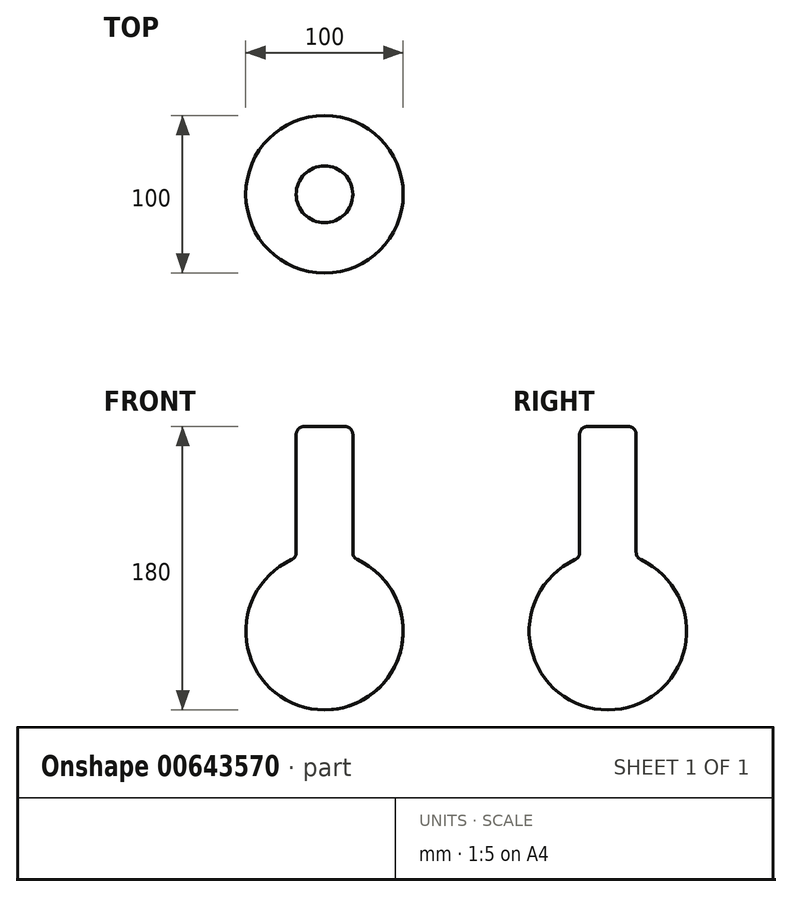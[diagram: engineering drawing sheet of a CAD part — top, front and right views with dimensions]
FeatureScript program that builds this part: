
annotation { "Feature Type Name" : "Feature", "Feature Type Description" : "" }
export const myFeature = defineFeature(function(context is Context, id is Id, definition is map)
    precondition{}
    {
        {
            var Q0;
            Q0=qCreatedBy(makeId("Front.planeOp"),FACE);
            var sketch = newSketch(context, id + "F0", { "sketchPlane" : qUnion([Q0])});
            skArc(sketch, "E0", {"start": v(0, 50) * mm, "mid": v(-50, 0) * mm, "end": v(0, -50) * mm});
            skLineSegment(sketch, "E1", {"start": v(0, 50) * mm, "end": v(0, -50) * mm});
            skSolve(sketch);
        }
        {
            var Q0;
            Q0 = qSketchRegion(id + "F0", true);
            var Q1;
            Q1=sQuery(id+"F0.wireOp",EDGE,"E1");
            revolve(context, id + "F1", {"entities" : qUnion([Q0]), "axis" : qUnion([Q1]), "revolveType" : RevolveType.FULL});
        }
        {
            var Q0;
            Q0=qCreatedBy(makeId("Top.planeOp"),FACE);
            var sketch = newSketch(context, id + "F2", { "sketchPlane" : qUnion([Q0])});
            skCircle(sketch, "E2", {"center": v(0, 0) * mm, "radius": 17.98 * mm});
            skSolve(sketch);
        }
        {
            var Q0;
            Q0 = qSketchRegion(id + "F2", true);
            extrude(context, id + "F3", {"entities" : qUnion([Q0]), "operationType" : NewBodyOperationType.ADD, "depth" : 130 * mm, "offsetDistance" : 25 * mm});
        }
        {
            var Q0;
            Q0=makeQuery(id+"F3.boolean.opBoolean","INTERSECT",EDGE,{"derivedFrom":[makeQuery(id+"F1.opRevolve","SWEPT_FACE",FACE,{"disambiguationData":[OSD([sQuery(id+"F0.wireOp",EDGE,"E0")])]}),makeQuery(id+"F3.opExtrude","SWEPT_FACE",FACE,{"disambiguationData":[OSD([sQuery(id+"F2.wireOp",EDGE,"E2")])]})]});
            fillet(context, id + "F4", {"entities" : qUnion([Q0]), "radius" : 5 * mm, "tangentPropagation" : true, "allowEdgeOverflow" : false});
        }
        {
            var Q0;
            Q0=makeQuery(id+"F3.opExtrude","CAP_EDGE",EDGE,{"disambiguationData":[OSD([sQuery(id+"F2.wireOp",EDGE,"E2")])],"isStart":false});
            fillet(context, id + "F5", {"entities" : qUnion([Q0]), "radius" : 5 * mm, "tangentPropagation" : true, "allowEdgeOverflow" : false});
        }
    });
